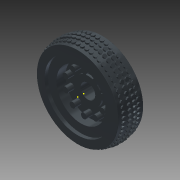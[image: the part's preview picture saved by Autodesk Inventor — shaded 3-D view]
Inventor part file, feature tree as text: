
AUTODESK INVENTOR PART (.ipt)
format: ipt  version: 2015 (Build 190159000, 159)  size: 3,271,168 bytes
history: native  units: in
note: dims shown in document units (in); Inventor stores cm internally (conversion verified against a paired STEP export)
features: other x3, sketch x3, extrude x1
ambient origin geometry x8: Origin, YZ Plane, XZ Plane, XY Plane, X Axis, Y Axis, Z Axis, Center Point
bodies: Solid1 (feature_tree)
feature tree (7):
  other  "Part3 (1).ipt"
  extrude  "Extrusion1"  Depth=0.3543in
  other  "Solid1::Part3 (1).ipt"
  other  "TaggingFeature1"
  sketch  "Sketch14"
  sketch  "Sketch3"  dims[d0=0.3543in d1=0.35in]
  sketch  "Sketch4"  dims[d2=1.0in d3=0.0in]
